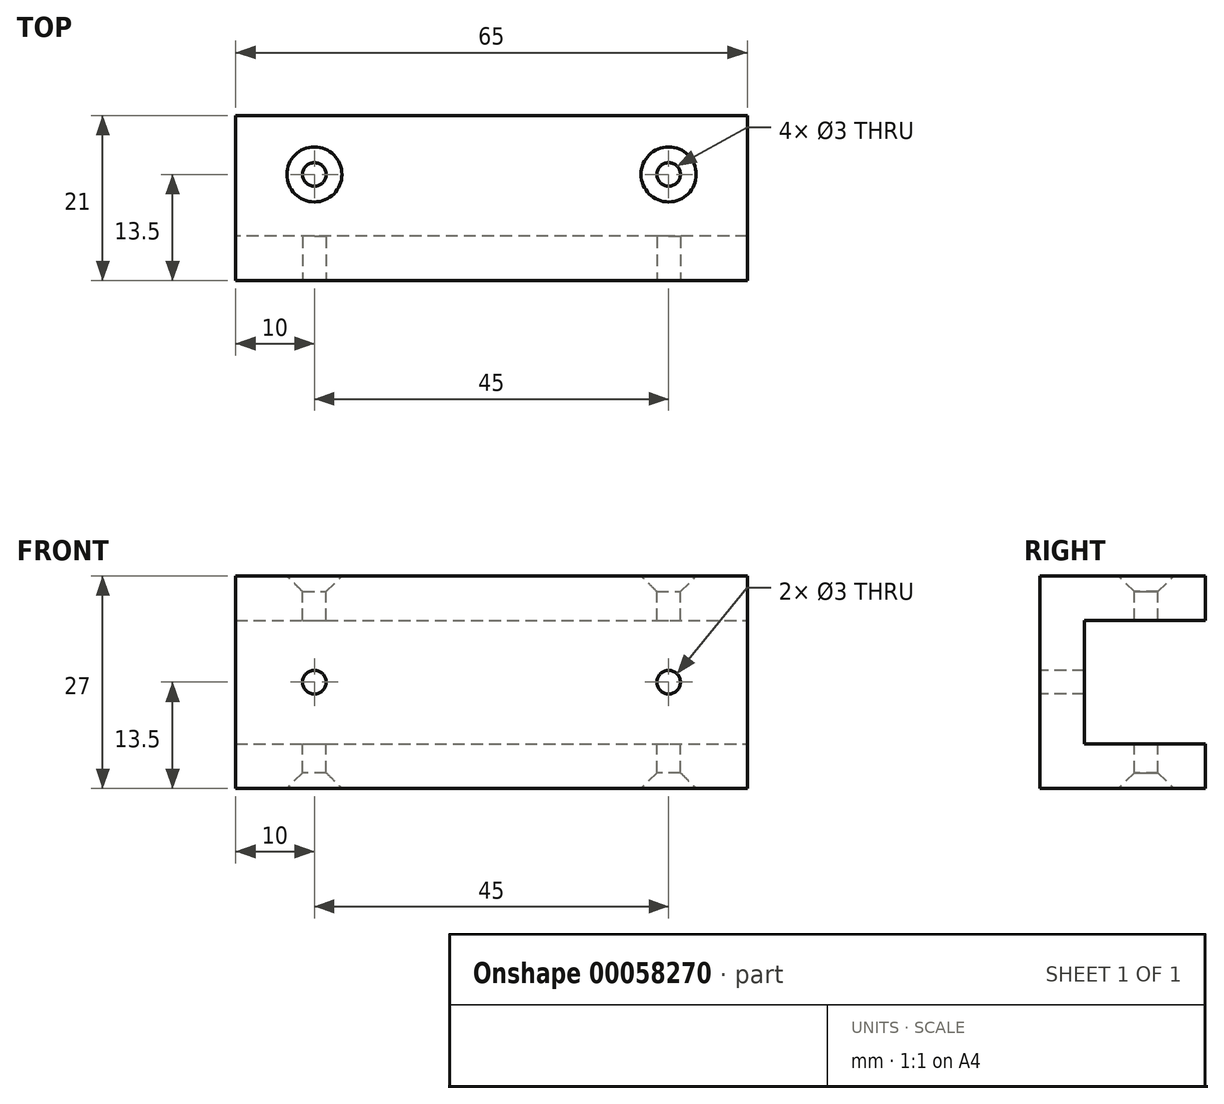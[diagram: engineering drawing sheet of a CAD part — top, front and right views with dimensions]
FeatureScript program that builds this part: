
annotation { "Feature Type Name" : "Feature", "Feature Type Description" : "" }
export const myFeature = defineFeature(function(context is Context, id is Id, definition is map)
    precondition{}
    {
        {
            var Q0;
            Q0=qCreatedBy(makeId("Right.planeOp"),FACE);
            var sketch = newSketch(context, id + "F0", { "sketchPlane" : qUnion([Q0])});
            skLineSegment(sketch, "E0.bottom", {"start": v(7.5, 7.5) * mm, "end": v(-7.5, 7.5) * mm});
            skLineSegment(sketch, "E0.top", {"start": v(7.5, -7.5) * mm, "end": v(-7.5, -7.5) * mm});
            skLineSegment(sketch, "E0.left", {"start": v(7.5, 7.5) * mm, "end": v(7.5, -7.5) * mm, "construction": true});
            skLineSegment(sketch, "E0.right", {"start": v(-7.5, 7.5) * mm, "end": v(-7.5, -7.5) * mm});
            skPoint(sketch, "E0.middle", {"position": v(0, 0) * mm});
            skLineSegment(sketch, "E1", {"start": v(7.5, 7.5) * mm, "end": v(7.5, 13.5) * mm});
            skLineSegment(sketch, "E2", {"start": v(7.5, 13.5) * mm, "end": v(-13.5, 13.5) * mm});
            skLineSegment(sketch, "E3", {"start": v(-13.5, 13.5) * mm, "end": v(-13.5, -13.5) * mm});
            skLineSegment(sketch, "E4", {"start": v(-13.5, -13.5) * mm, "end": v(7.5, -13.5) * mm});
            skLineSegment(sketch, "E5", {"start": v(7.5, -13.5) * mm, "end": v(7.5, -7.5) * mm});
            skSolve(sketch);
        }
        {
            var Q0;
            Q0 = qSketchRegion(id + "F0", true);
            extrude(context, id + "F1", {"entities" : qUnion([Q0]), "depth" : 65 * mm});
        }
        {
            var Q0;
            Q0=makeQuery(id+"F1.opExtrude","SWEPT_FACE",FACE,{"disambiguationData":[OSD([sQuery(id+"F0.wireOp",EDGE,"E3")])]});
            var sketch = newSketch(context, id + "F2", { "sketchPlane" : qUnion([Q0])});
            skLineSegment(sketch, "E6", {"start": v(0, 0) * mm, "end": v(65, 0) * mm, "construction": true});
            skCircle(sketch, "E7", {"center": v(10, 0) * mm, "radius": 1.5 * mm});
            skCircle(sketch, "E8", {"center": v(55, 0) * mm, "radius": 1.5 * mm});
            skSolve(sketch);
        }
        {
            var Q0;
            Q0 = qSketchRegion(id + "F2", true);
            extrude(context, id + "F3", {"entities" : qUnion([Q0]), "operationType" : NewBodyOperationType.REMOVE, "endBound" : BoundingType.THROUGH_ALL, "oppositeDirection" : true, "depth" : 25 * mm});
        }
        {
            var Q0;
            Q0=makeQuery(id+"F1.opExtrude","SWEPT_FACE",FACE,{"disambiguationData":[OSD([sQuery(id+"F0.wireOp",EDGE,"E0.bottom")])]});
            var sketch = newSketch(context, id + "F4", { "sketchPlane" : qUnion([Q0])});
            skLineSegment(sketch, "E9", {"start": v(65, 0) * mm, "end": v(0, 0) * mm, "construction": true});
            skCircle(sketch, "E10", {"center": v(55, 0) * mm, "radius": 1.5 * mm});
            skCircle(sketch, "E11", {"center": v(10, 0) * mm, "radius": 1.5 * mm});
            skSolve(sketch);
        }
        {
            var Q0;
            Q0 = qSketchRegion(id + "F4", true);
            extrude(context, id + "F5", {"entities" : qUnion([Q0]), "operationType" : NewBodyOperationType.REMOVE, "endBound" : BoundingType.THROUGH_ALL, "depth" : 25 * mm, "hasSecondDirection" : true, "secondDirectionBound" : BoundingType.THROUGH_ALL, "secondDirectionOppositeDirection" : true, "secondDirectionDepth" : 25 * mm});
        }
        {
            var Q0;
            Q0=makeQuery(id+"F5.boolean.opBoolean","INTERSECT",EDGE,{"derivedFrom":[makeQuery(id+"F1.opExtrude","SWEPT_FACE",FACE,{"disambiguationData":[OSD([sQuery(id+"F0.wireOp",EDGE,"E4")])]}),makeQuery(id+"F5.opExtrude","SWEPT_FACE",FACE,{"disambiguationData":[OSD([sQuery(id+"F4.wireOp",EDGE,"E10")])]})]});
            var Q1;
            Q1=makeQuery(id+"F5.boolean.opBoolean","INTERSECT",EDGE,{"derivedFrom":[makeQuery(id+"F1.opExtrude","SWEPT_FACE",FACE,{"disambiguationData":[OSD([sQuery(id+"F0.wireOp",EDGE,"E4")])]}),makeQuery(id+"F5.opExtrude","SWEPT_FACE",FACE,{"disambiguationData":[OSD([sQuery(id+"F4.wireOp",EDGE,"E11")])]})]});
            var Q2;
            Q2=makeQuery(id+"F5.boolean.opBoolean","INTERSECT",EDGE,{"derivedFrom":[makeQuery(id+"F1.opExtrude","SWEPT_FACE",FACE,{"disambiguationData":[OSD([sQuery(id+"F0.wireOp",EDGE,"E2")])]}),makeQuery(id+"F5.opExtrude","SWEPT_FACE",FACE,{"disambiguationData":[OSD([sQuery(id+"F4.wireOp",EDGE,"E10")])]})]});
            var Q3;
            Q3=makeQuery(id+"F5.boolean.opBoolean","INTERSECT",EDGE,{"derivedFrom":[makeQuery(id+"F1.opExtrude","SWEPT_FACE",FACE,{"disambiguationData":[OSD([sQuery(id+"F0.wireOp",EDGE,"E2")])]}),makeQuery(id+"F5.opExtrude","SWEPT_FACE",FACE,{"disambiguationData":[OSD([sQuery(id+"F4.wireOp",EDGE,"E11")])]})]});
            var Q4;
            Q4=makeQuery(id+"F3.boolean.opBoolean","COPY",EDGE,{"derivedFrom":makeQuery(id+"F3.opExtrude","CAP_EDGE",EDGE,{"disambiguationData":[OSD([sQuery(id+"F2.wireOp",EDGE,"E7")])],"isStart":true})});
            var Q5;
            Q5=makeQuery(id+"F3.boolean.opBoolean","COPY",EDGE,{"derivedFrom":makeQuery(id+"F3.opExtrude","CAP_EDGE",EDGE,{"disambiguationData":[OSD([sQuery(id+"F2.wireOp",EDGE,"E8")])],"isStart":true})});
            chamfer(context, id + "F6", {"entities" : qUnion([Q0, Q1, Q2, Q3, Q4, Q5]), "width" : 2 * mm, "tangentPropagation" : true});
        }
        {
            var Q0;
            Q0=makeQuery(id+"F1.opExtrude","CAP_FACE",FACE,{"disambiguationData":[OSD([sQuery(id+"F0.wireOp",EDGE,"E0.bottom"),sQuery(id+"F0.wireOp",EDGE,"E0.top"),sQuery(id+"F0.wireOp",EDGE,"E0.right"),sQuery(id+"F0.wireOp",EDGE,"E1"),sQuery(id+"F0.wireOp",EDGE,"E2"),sQuery(id+"F0.wireOp",EDGE,"E3"),sQuery(id+"F0.wireOp",EDGE,"E4"),sQuery(id+"F0.wireOp",EDGE,"E5")])],"isStart":true});
            var sketch = newSketch(context, id + "F7", { "sketchPlane" : qUnion([Q0])});
            skLineSegment(sketch, "E12", {"start": v(-7.5, -7.5) * mm, "end": v(7.5, 7.5) * mm, "construction": true});
            skLineSegment(sketch, "E13.bottom", {"start": v(-7.85, 7.85) * mm, "end": v(7.85, 7.85) * mm});
            skLineSegment(sketch, "E13.top", {"start": v(-7.85, -7.85) * mm, "end": v(7.85, -7.85) * mm});
            skLineSegment(sketch, "E13.left", {"start": v(-7.85, 7.85) * mm, "end": v(-7.85, -7.85) * mm});
            skLineSegment(sketch, "E13.right", {"start": v(7.85, 7.85) * mm, "end": v(7.85, -7.85) * mm});
            skPoint(sketch, "E13.middle", {"position": v(0, 0) * mm});
            skSolve(sketch);
        }
        {
            var Q0;
            Q0 = qSketchRegion(id + "F7", true);
            extrude(context, id + "F8", {"entities" : qUnion([Q0]), "operationType" : NewBodyOperationType.REMOVE, "endBound" : BoundingType.THROUGH_ALL, "oppositeDirection" : true, "depth" : 25 * mm});
        }
    });
